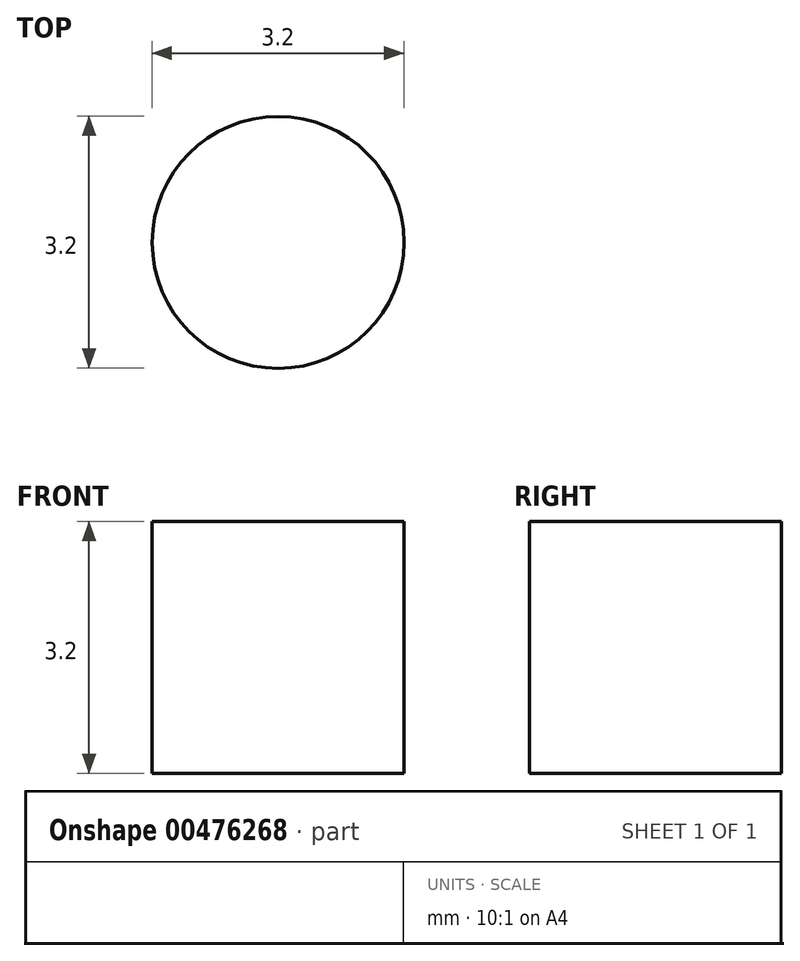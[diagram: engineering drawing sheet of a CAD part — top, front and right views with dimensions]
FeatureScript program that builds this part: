
annotation { "Feature Type Name" : "Feature", "Feature Type Description" : "" }
export const myFeature = defineFeature(function(context is Context, id is Id, definition is map)
    precondition{}
    {
        {
            var Q0;
            Q0=qCreatedBy(makeId("Top.planeOp"),FACE);
            var sketch = newSketch(context, id + "F0", { "sketchPlane" : qUnion([Q0])});
            skCircle(sketch, "E0", {"center": v(-47.13, -31.95) * mm, "radius": 1.6 * mm});
            skSolve(sketch);
        }
        {
            var Q0;
            Q0=makeQuery(id+"F0.imprint","IMPRINT",FACE,{"disambiguationData":[TD([[makeQuery(id+"F0.imprint","IMPRINT",EDGE,{"derivedFrom":sQuery(id+"F0.wireOp",EDGE,"E0")}),1.0]])]});
            extrude(context, id + "F1", {"entities" : qUnion([Q0]), "depth" : 3.2 * mm, "offsetDistance" : 25 * mm});
        }
    });
